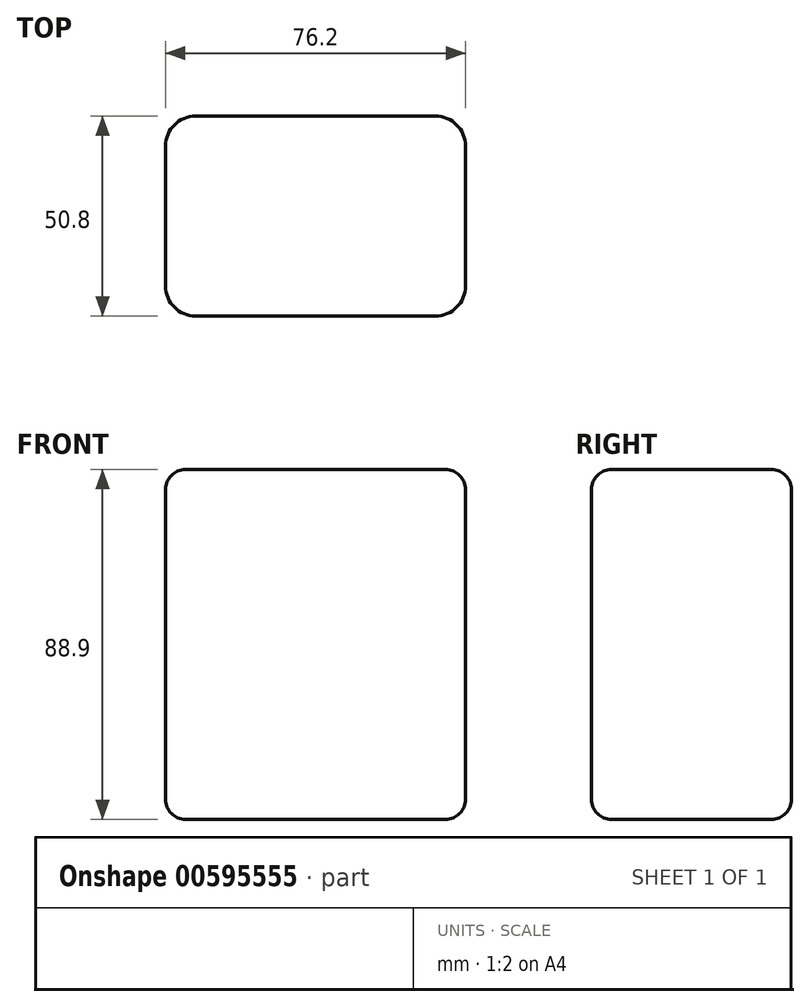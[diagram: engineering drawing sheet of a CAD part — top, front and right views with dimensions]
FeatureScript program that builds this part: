
annotation { "Feature Type Name" : "Feature", "Feature Type Description" : "" }
export const myFeature = defineFeature(function(context is Context, id is Id, definition is map)
    precondition{}
    {
        {
            var Q0;
            Q0=qCreatedBy(makeId("Top.planeOp"),FACE);
            var sketch = newSketch(context, id + "F0", { "sketchPlane" : qUnion([Q0])});
            skLineSegment(sketch, "E0.bottom", {"start": v(-30.48, 25.4) * mm, "end": v(30.48, 25.4) * mm});
            skLineSegment(sketch, "E0.top", {"start": v(-30.48, -25.4) * mm, "end": v(30.48, -25.4) * mm});
            skLineSegment(sketch, "E0.left", {"start": v(-38.1, 17.78) * mm, "end": v(-38.1, -17.78) * mm});
            skLineSegment(sketch, "E0.right", {"start": v(38.1, 17.78) * mm, "end": v(38.1, -17.78) * mm});
            skPoint(sketch, "E0.middle", {"position": v(0, 0) * mm});
            skPoint(sketch, "E1.visualSharp", {"position": v(-38.1, 25.4) * mm});
            skPoint(sketch, "E2.visualSharp", {"position": v(-38.1, -25.4) * mm});
            skArc(sketch, "E2.filletArc", {"start": v(-38.1, -17.78) * mm, "mid": v(-35.87, -23.17) * mm, "end": v(-30.48, -25.4) * mm});
            skPoint(sketch, "E3.visualSharp", {"position": v(38.1, -25.4) * mm});
            skArc(sketch, "E3.filletArc", {"start": v(30.48, -25.4) * mm, "mid": v(35.87, -23.17) * mm, "end": v(38.1, -17.78) * mm});
            skPoint(sketch, "E4.visualSharp", {"position": v(38.1, 25.4) * mm});
            skArc(sketch, "E4.filletArc", {"start": v(38.1, 17.78) * mm, "mid": v(35.87, 23.17) * mm, "end": v(30.48, 25.4) * mm});
            skArc(sketch, "E5.filletArc", {"start": v(-30.48, 25.4) * mm, "mid": v(-35.87, 23.17) * mm, "end": v(-38.1, 17.78) * mm});
            skSolve(sketch);
        }
        {
            var Q0;
            Q0=makeQuery(id+"F0.imprint","IMPRINT",FACE,{"disambiguationData":[TD([[makeQuery(id+"F0.imprint","IMPRINT",EDGE,{"derivedFrom":sQuery(id+"F0.wireOp",EDGE,"E0.bottom")}),-1.0]])]});
            extrude(context, id + "F1", {"entities" : qUnion([Q0]), "depth" : 88.9 * mm, "offsetDistance" : 25.4 * mm});
        }
        {
            var Q0;
            Q0=makeQuery(id+"F1.opExtrude","CAP_FACE",FACE,{"disambiguationData":[OSD([sQuery(id+"F0.wireOp",EDGE,"E0.bottom"),sQuery(id+"F0.wireOp",EDGE,"E0.top"),sQuery(id+"F0.wireOp",EDGE,"E0.left"),sQuery(id+"F0.wireOp",EDGE,"E0.right"),sQuery(id+"F0.wireOp",EDGE,"E2.filletArc"),sQuery(id+"F0.wireOp",EDGE,"E3.filletArc"),sQuery(id+"F0.wireOp",EDGE,"E4.filletArc"),sQuery(id+"F0.wireOp",EDGE,"E5.filletArc")])],"isStart":false});
            var Q1;
            Q1=makeQuery(id+"F1.opExtrude","CAP_FACE",FACE,{"disambiguationData":[OSD([sQuery(id+"F0.wireOp",EDGE,"E0.bottom"),sQuery(id+"F0.wireOp",EDGE,"E0.top"),sQuery(id+"F0.wireOp",EDGE,"E0.left"),sQuery(id+"F0.wireOp",EDGE,"E0.right"),sQuery(id+"F0.wireOp",EDGE,"E2.filletArc"),sQuery(id+"F0.wireOp",EDGE,"E3.filletArc"),sQuery(id+"F0.wireOp",EDGE,"E4.filletArc"),sQuery(id+"F0.wireOp",EDGE,"E5.filletArc")])],"isStart":true});
            fillet(context, id + "F2", {"entities" : qUnion([Q0, Q1]), "radius" : 5.08 * mm, "tangentPropagation" : true, "allowEdgeOverflow" : false});
        }
    });
